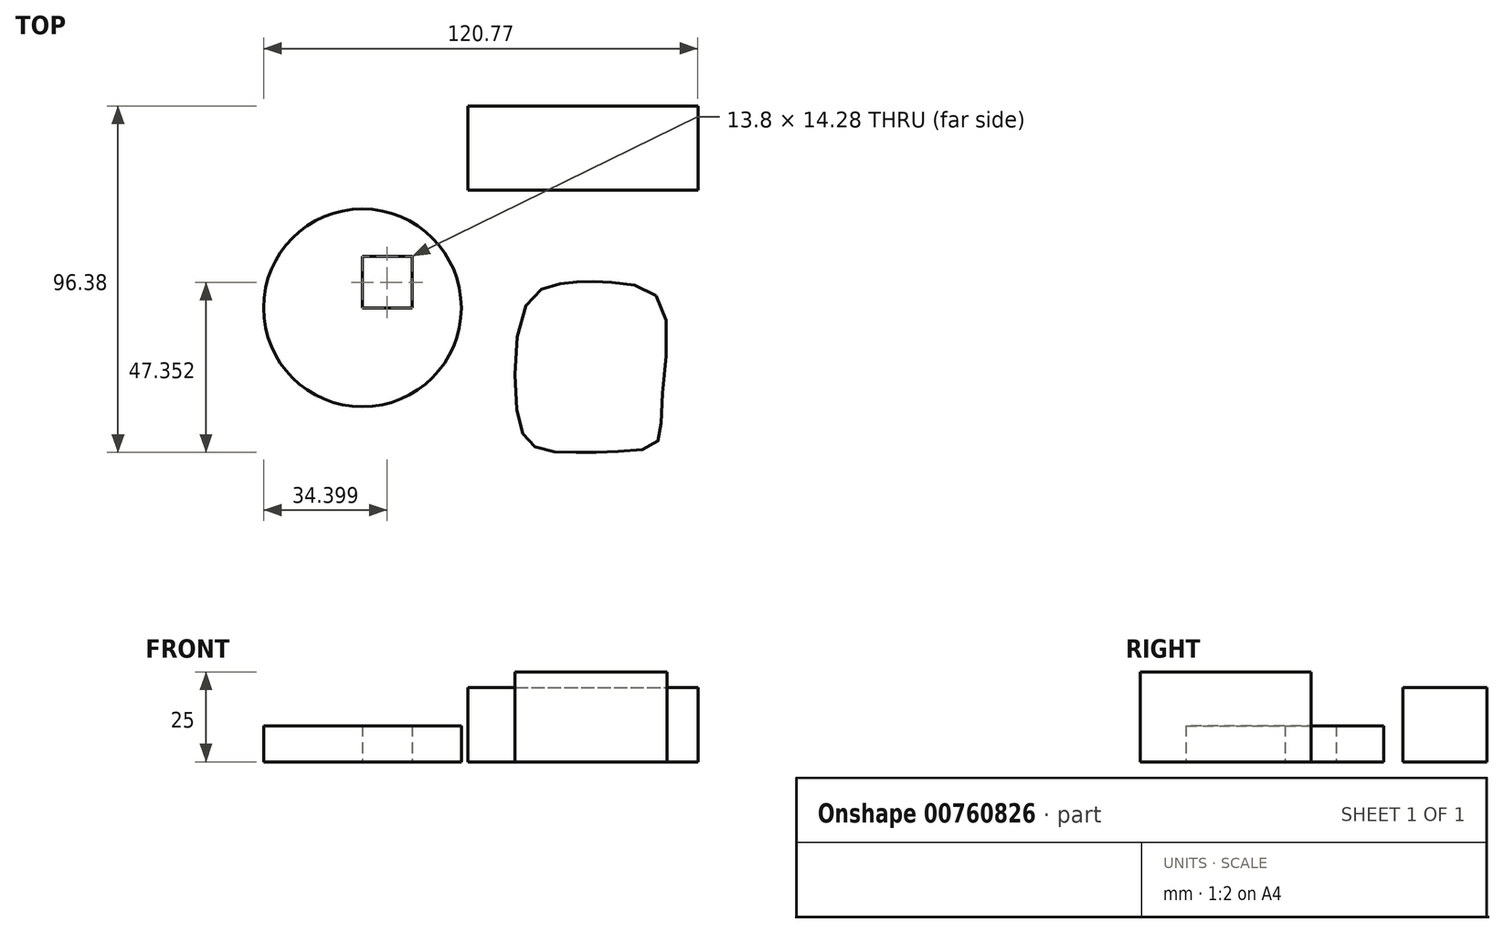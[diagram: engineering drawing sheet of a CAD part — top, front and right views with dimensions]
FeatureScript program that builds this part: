
annotation { "Feature Type Name" : "Feature", "Feature Type Description" : "" }
export const myFeature = defineFeature(function(context is Context, id is Id, definition is map)
    precondition{}
    {
        {
            var Q0;
            Q0=qCreatedBy(makeId("Top.planeOp"),FACE);
            var sketch = newSketch(context, id + "F0", { "sketchPlane" : qUnion([Q0])});
            skCircle(sketch, "E0", {"center": v(-25.54, -16.22) * mm, "radius": 27.5 * mm});
            skLineSegment(sketch, "E1.bottom", {"start": v(-25.54, -16.22) * mm, "end": v(-11.74, -16.22) * mm});
            skLineSegment(sketch, "E1.top", {"start": v(-25.54, -1.94) * mm, "end": v(-11.74, -1.94) * mm});
            skLineSegment(sketch, "E1.left", {"start": v(-25.54, -16.22) * mm, "end": v(-25.54, -1.94) * mm});
            skLineSegment(sketch, "E1.right", {"start": v(-11.74, -16.22) * mm, "end": v(-11.74, -1.94) * mm});
            skSolve(sketch);
        }
        {
            var Q0;
            Q0=makeQuery(id+"F0.imprint","IMPRINT",FACE,{"disambiguationData":[TD([[makeQuery(id+"F0.imprint","IMPRINT",EDGE,{"derivedFrom":sQuery(id+"F0.wireOp",EDGE,"E0")}),1.0]])]});
            extrude(context, id + "F1", {"entities" : qUnion([Q0]), "depth" : 10 * mm, "offsetDistance" : 25 * mm});
        }
        {
            var Q0;
            Q0=qCreatedBy(makeId("Top.planeOp"),FACE);
            var sketch = newSketch(context, id + "F2", { "sketchPlane" : qUnion([Q0])});
            skLineSegment(sketch, "E2.bottom", {"start": v(3.74, 39.95) * mm, "end": v(67.73, 39.95) * mm});
            skLineSegment(sketch, "E2.top", {"start": v(3.74, 16.57) * mm, "end": v(67.73, 16.57) * mm});
            skLineSegment(sketch, "E2.left", {"start": v(3.74, 39.95) * mm, "end": v(3.74, 16.57) * mm});
            skLineSegment(sketch, "E2.right", {"start": v(67.73, 39.95) * mm, "end": v(67.73, 16.57) * mm});
            skSolve(sketch);
        }
        {
            var Q0;
            Q0=makeQuery(id+"F2.imprint","IMPRINT",FACE,{"disambiguationData":[TD([[makeQuery(id+"F2.imprint","IMPRINT",EDGE,{"derivedFrom":sQuery(id+"F2.wireOp",EDGE,"E2.bottom")}),-1.0]])]});
            extrude(context, id + "F3", {"entities" : qUnion([Q0]), "depth" : 20.6 * mm, "offsetDistance" : 25 * mm});
        }
        {
            var Q0;
            Q0=qCreatedBy(makeId("Top.planeOp"),FACE);
            var sketch = newSketch(context, id + "F4", { "sketchPlane" : qUnion([Q0])});
            skCircle(sketch, "E3", {"center": v(23.85, 31.33) * mm, "radius": 6.37 * mm});
            skCircle(sketch, "E4", {"center": v(23.85, 31.33) * mm, "radius": 6.4 * mm});
            skSolve(sketch);
        }
        {
            var Q0;
            Q0=sQuery(id+"F4.wireOp",EDGE,"E4");
            extrude(context, id + "F5", {"bodyType" : ToolBodyType.SURFACE, "surfaceEntities" : qUnion([Q0]), "depth" : 58.6 * mm, "offsetDistance" : 25 * mm});
        }
        {
            var Q0;
            Q0=qCreatedBy(makeId("Right.planeOp"),FACE);
            var sketch = newSketch(context, id + "F6", { "sketchPlane" : qUnion([Q0])});
            skCircle(sketch, "E5", {"center": v(31.52, 40.33) * mm, "radius": 5.3 * mm});
            skSolve(sketch);
        }
        {
            var Q0;
            Q0=sQuery(id+"F6.wireOp",EDGE,"E5");
            extrude(context, id + "F7", {"bodyType" : ToolBodyType.SURFACE, "surfaceEntities" : qUnion([Q0]), "depth" : 56.9 * mm, "offsetDistance" : 25 * mm});
        }
        {
            var Q0;
            Q0=qCreatedBy(makeId("Top.planeOp"),FACE);
            var sketch = newSketch(context, id + "F8", { "sketchPlane" : qUnion([Q0])});
            skFitSpline(sketch, "E6", {"points": [v(29.41, -9.48) * mm, v(20.6, -14.47) * mm, v(17.34, -44.17) * mm, v(22.13, -54.7) * mm, v(32.86, -56.43) * mm, v(43.6, -56.24) * mm, v(55.85, -54.13) * mm, v(57.58, -43.97) * mm, v(57.39, -14.47) * mm, v(45.12, -9.3) * mm, v(36.5, -8.9) * mm, v(29.41, -9.48) * mm]});
            skSolve(sketch);
        }
        {
            var Q0;
            Q0=makeQuery(id+"F8.imprint","IMPRINT",FACE,{"disambiguationData":[TD([[makeQuery(id+"F8.imprint","IMPRINT",EDGE,{"derivedFrom":sQuery(id+"F8.wireOp",EDGE,"E6")}),1.0]])]});
            extrude(context, id + "F9", {"entities" : qUnion([Q0]), "depth" : 25 * mm, "offsetDistance" : 25 * mm});
        }
    });
